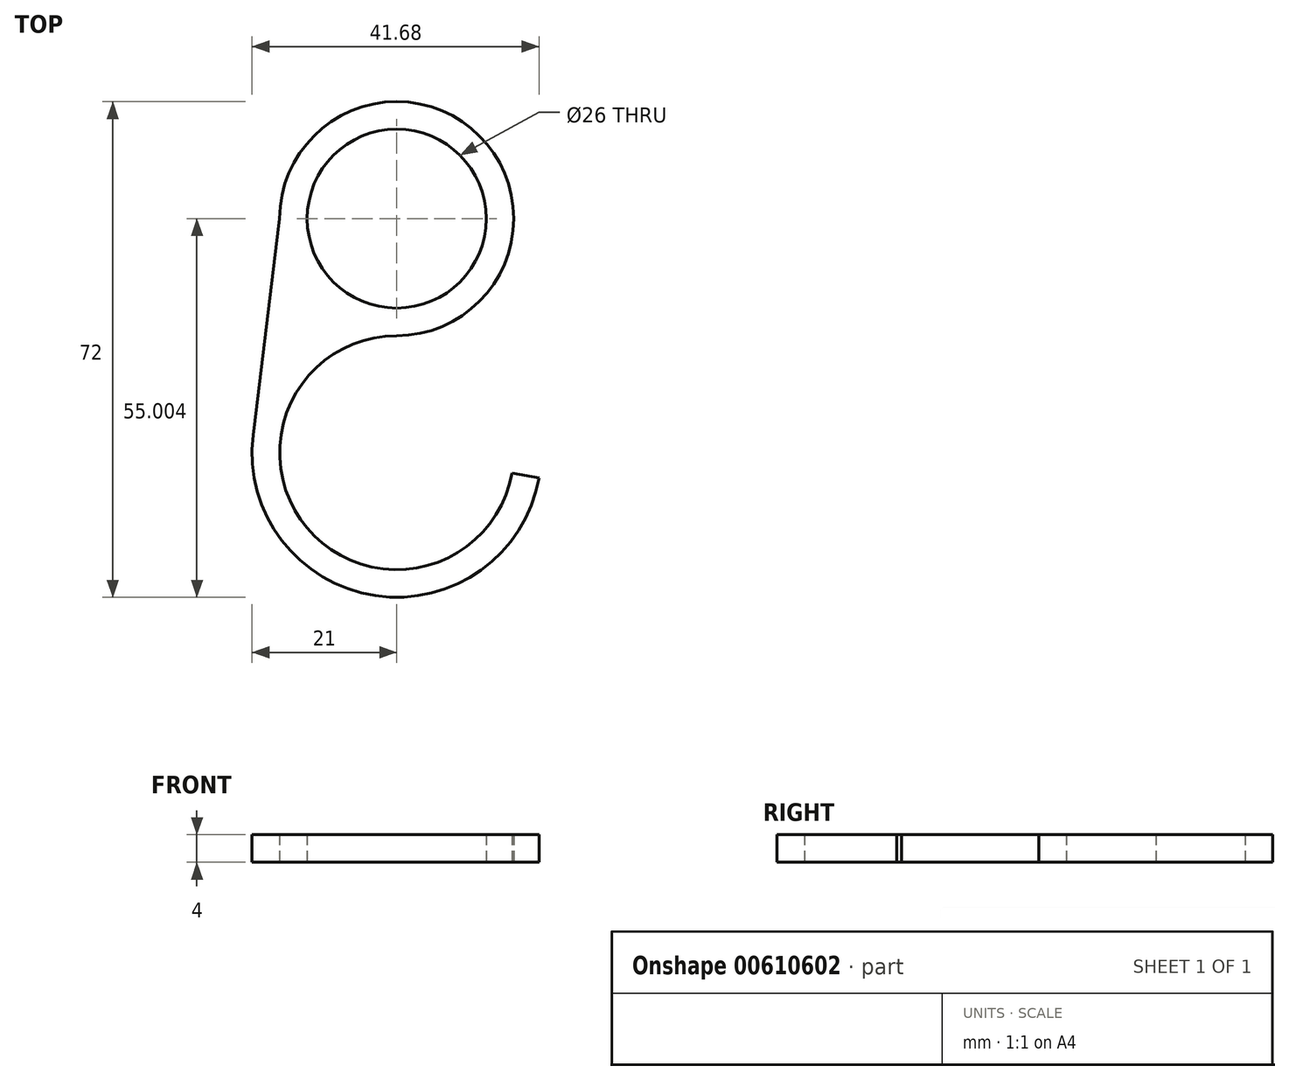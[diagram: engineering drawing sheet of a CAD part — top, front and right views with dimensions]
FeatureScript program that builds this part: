
annotation { "Feature Type Name" : "Feature", "Feature Type Description" : "" }
export const myFeature = defineFeature(function(context is Context, id is Id, definition is map)
    precondition{}
    {
        {
            var Q0;
            Q0=qCreatedBy(makeId("Top.planeOp"),FACE);
            var sketch = newSketch(context, id + "F0", { "sketchPlane" : qUnion([Q0])});
            skCircle(sketch, "E0", {"center": v(0, 22.31) * mm, "radius": 13 * mm});
            skArc(sketch, "E1", {"start": v(0, 5.31) * mm, "mid": v(-13.02, -22.61) * mm, "end": v(16.74, -14.64) * mm});
            skArc(sketch, "E2", {"start": v(0, 5.31) * mm, "mid": v(12.02, 34.33) * mm, "end": v(-17, 22.31) * mm});
            skArc(sketch, "E3", {"start": v(-20.84, -9.14) * mm, "mid": v(-3.1, -32.46) * mm, "end": v(20.68, -15.33) * mm});
            skPoint(sketch, "E4", {"position": v(0, 39.31) * mm});
            skPoint(sketch, "E5", {"position": v(0, -32.69) * mm});
            skLineSegment(sketch, "E6", {"start": v(-17, 22.31) * mm, "end": v(-21.16, -11.69) * mm});
            skLineSegment(sketch, "E7", {"start": v(0, -11.69) * mm, "end": v(20.68, -15.33) * mm});
            skLineSegment(sketch, "E8", {"start": v(20.68, -15.33) * mm, "end": v(18.71, -14.99) * mm});
            skArc(sketch, "E9", {"start": v(20.68, -15.33) * mm, "mid": v(19.06, -13.02) * mm, "end": v(16.74, -14.64) * mm});
            skSolve(sketch);
        }
        {
            var Q0;
            Q0=makeQuery(id+"F0.imprint","IMPRINT",FACE,{"disambiguationData":[TD([[makeQuery(id+"F0.imprint","IMPRINT",EDGE,{"derivedFrom":sQuery(id+"F0.wireOp",EDGE,"E0")}),-1.0]])]});
            var Q1;
            {var subQ2=sQuery(id+"F0.wireOp",EDGE,"E8");Q1=makeQuery(id+"F0.imprint","IMPRINT",FACE,{"disambiguationData":[TD([[makeQuery(id+"F0.imprint","IMPRINT",EDGE,{"derivedFrom":subQ2}),-1.0]])]});}
            extrude(context, id + "F1", {"entities" : qUnion([Q0, Q1]), "depth" : 4 * mm, "offsetDistance" : 25 * mm});
        }
    });
